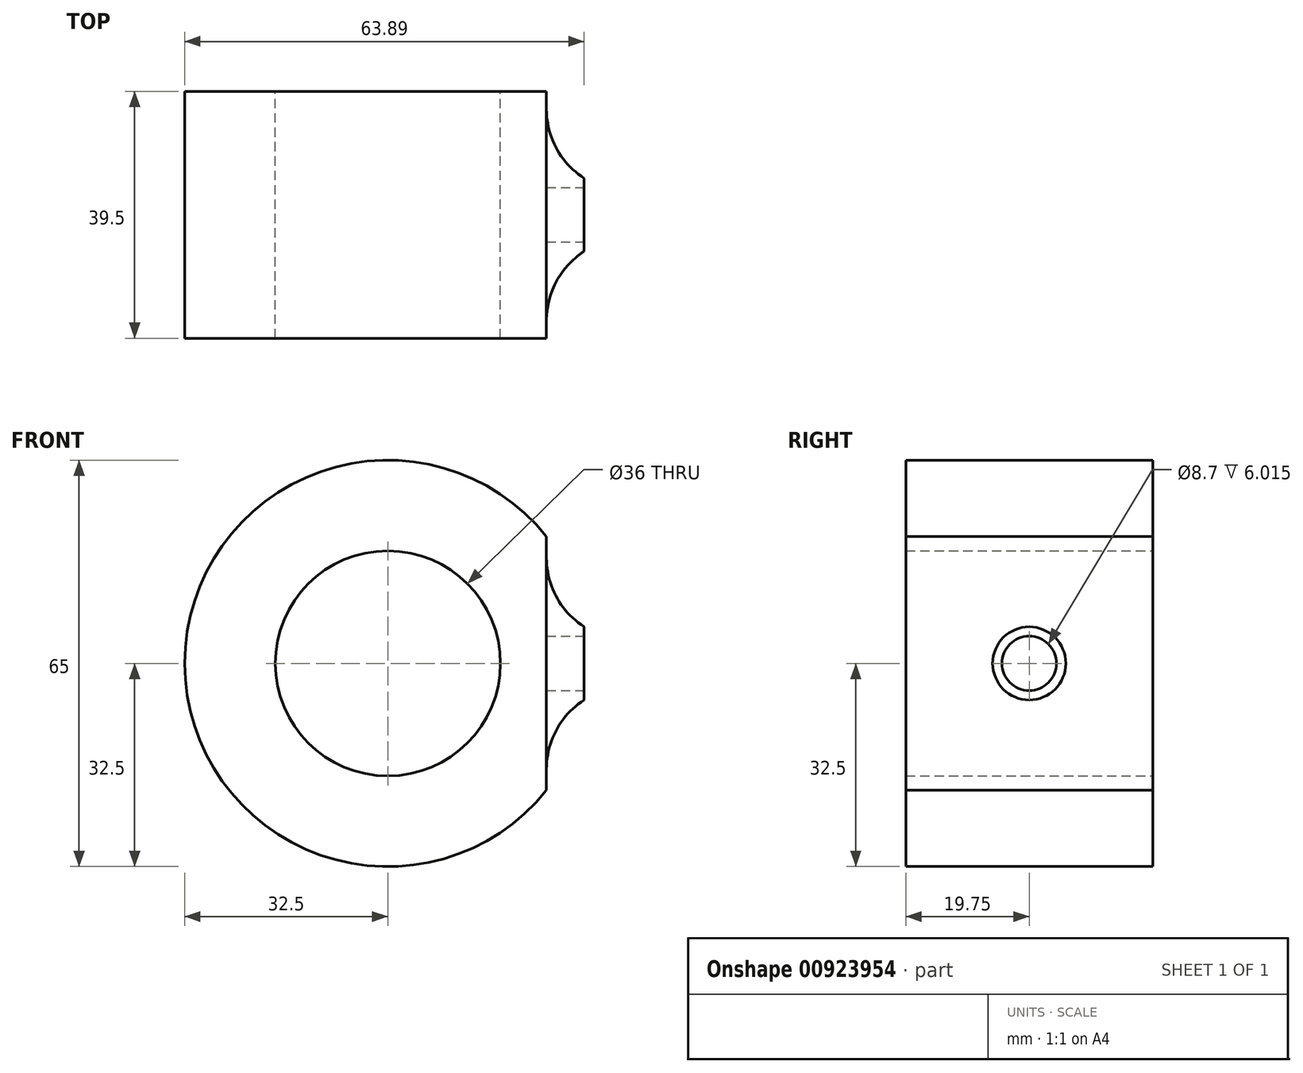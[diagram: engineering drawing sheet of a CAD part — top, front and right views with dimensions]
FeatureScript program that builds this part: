
annotation { "Feature Type Name" : "Feature", "Feature Type Description" : "" }
export const myFeature = defineFeature(function(context is Context, id is Id, definition is map)
    precondition{}
    {
        {
            var Q0;
            Q0=qCreatedBy(makeId("Front.planeOp"),FACE);
            var sketch = newSketch(context, id + "F0", { "sketchPlane" : qUnion([Q0])});
            skCircle(sketch, "E0", {"center": v(0, 0) * mm, "radius": 32.5 * mm});
            skCircle(sketch, "E1", {"center": v(0, 0) * mm, "radius": 18 * mm});
            skSolve(sketch);
        }
        {
            var Q0;
            Q0 = qSketchRegion(id + "F0", true);
            extrude(context, id + "F1", {"entities" : qUnion([Q0]), "depth" : 39.5 * mm, "offsetDistance" : 25 * mm});
        }
        {
            var Q0;
            Q0=qCreatedBy(makeId("Top.planeOp"),FACE);
            var sketch = newSketch(context, id + "F2", { "sketchPlane" : qUnion([Q0])});
            skLineSegment(sketch, "E2", {"start": v(-37.27, -19.75) * mm, "end": v(48.27, -19.75) * mm, "construction": true});
            skLineSegment(sketch, "E3", {"start": v(25.37, -15.4) * mm, "end": v(25.37, -19.75) * mm});
            skLineSegment(sketch, "E4", {"start": v(25.37, -19.75) * mm, "end": v(38.3, -19.75) * mm});
            skLineSegment(sketch, "E5", {"start": v(38.3, -19.75) * mm, "end": v(38.3, 9.95) * mm});
            skLineSegment(sketch, "E6", {"start": v(38.3, 9.95) * mm, "end": v(25.37, 9.95) * mm});
            skLineSegment(sketch, "E7", {"start": v(25.37, -15.4) * mm, "end": v(31.39, -15.4) * mm});
            skLineSegment(sketch, "E8", {"start": v(31.39, -15.4) * mm, "end": v(31.39, -13.9) * mm});
            skLineSegment(sketch, "E9", {"start": v(25.37, 9.95) * mm, "end": v(25.37, -2.86) * mm});
            skArc(sketch, "E10", {"start": v(25.37, -2.86) * mm, "mid": v(26.98, -9.14) * mm, "end": v(31.39, -13.9) * mm});
            skSolve(sketch);
        }
        {
            var Q0;
            Q0=makeQuery(id+"F2.imprint","IMPRINT",FACE,{"disambiguationData":[TD([[makeQuery(id+"F2.imprint","IMPRINT",EDGE,{"derivedFrom":sQuery(id+"F2.wireOp",EDGE,"E3")}),1.0]])]});
            var Q1;
            Q1=sQuery(id+"F2.wireOp",EDGE,"E2");
            revolve(context, id + "F3", {"operationType" : NewBodyOperationType.REMOVE, "surfaceOperationType" : NewSurfaceOperationType.NEW, "entities" : qUnion([Q0]), "axis" : qUnion([Q1]), "revolveType" : RevolveType.FULL, "oppositeDirection" : true});
        }
    });
